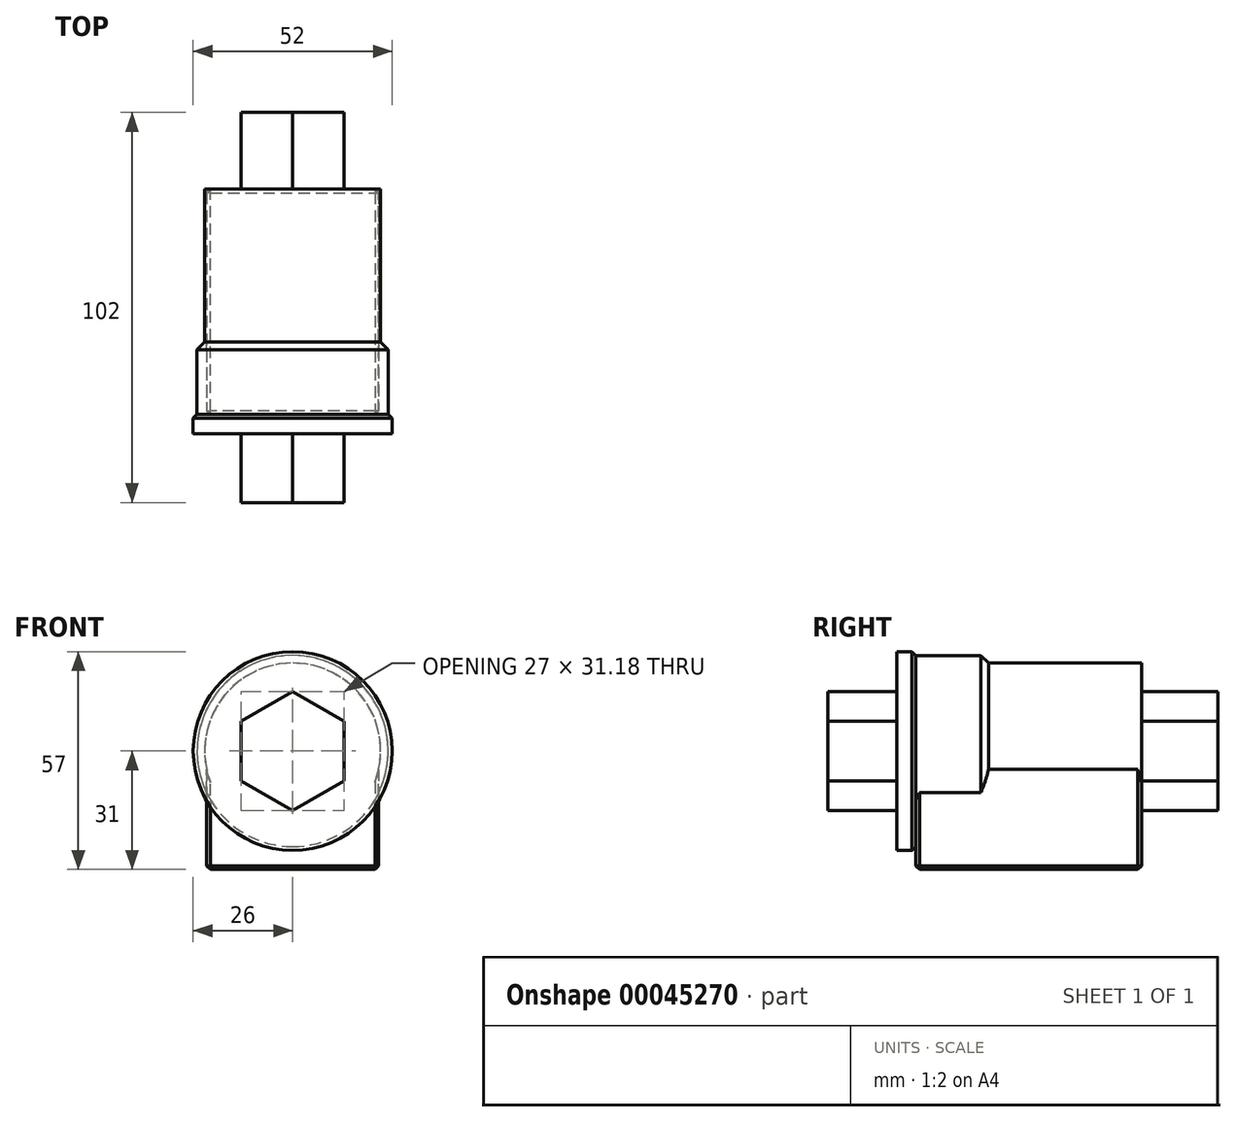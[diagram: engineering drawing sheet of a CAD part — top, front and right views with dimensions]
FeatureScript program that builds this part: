
annotation { "Feature Type Name" : "Feature", "Feature Type Description" : "" }
export const myFeature = defineFeature(function(context is Context, id is Id, definition is map)
    precondition{}
    {
        {
            var Q0;
            Q0=qCreatedBy(makeId("Front.planeOp"),FACE);
            var sketch = newSketch(context, id + "F0", { "sketchPlane" : qUnion([Q0])});
            skCircle(sketch, "E0", {"center": v(0, 0) * mm, "radius": 23 * mm});
            skCircle(sketch, "E1", {"center": v(0, 0) * mm, "radius": 26 * mm});
            skCircle(sketch, "E2", {"center": v(0, 0) * mm, "radius": 25 * mm});
            skCircle(sketch, "E3.cCircle", {"center": v(0, 0) * mm, "radius": 13.5 * mm, "construction": true});
            skLineSegment(sketch, "E3.0", {"start": v(13.5, 7.8) * mm, "end": v(13.5, -7.8) * mm});
            skLineSegment(sketch, "E3.1", {"start": v(13.5, -7.8) * mm, "end": v(0, -15.59) * mm});
            skLineSegment(sketch, "E3.2", {"start": v(0, -15.59) * mm, "end": v(-13.5, -7.8) * mm});
            skLineSegment(sketch, "E3.3", {"start": v(-13.5, -7.8) * mm, "end": v(-13.5, 7.8) * mm});
            skLineSegment(sketch, "E3.4", {"start": v(-13.5, 7.8) * mm, "end": v(0, 15.59) * mm});
            skLineSegment(sketch, "E3.5", {"start": v(0, 15.59) * mm, "end": v(13.5, 7.8) * mm});
            skPoint(sketch, "E3.0.midPoint", {"position": v(13.5, 0) * mm});
            skSolve(sketch);
        }
        {
            var Q0;
            Q0=makeQuery(id+"F0.imprint","IMPRINT",FACE,{"disambiguationData":[TD([[makeQuery(id+"F0.imprint","IMPRINT",EDGE,{"derivedFrom":sQuery(id+"F0.wireOp",EDGE,"E1")}),1.0]])]});
            var Q1;
            Q1=makeQuery(id+"F0.imprint","IMPRINT",FACE,{"disambiguationData":[TD([[makeQuery(id+"F0.imprint","IMPRINT",EDGE,{"derivedFrom":sQuery(id+"F0.wireOp",EDGE,"E0")}),-1.0]])]});
            var Q2;
            Q2=makeQuery(id+"F0.imprint","IMPRINT",FACE,{"disambiguationData":[TD([[makeQuery(id+"F0.imprint","IMPRINT",EDGE,{"derivedFrom":sQuery(id+"F0.wireOp",EDGE,"E0")}),1.0]])]});
            extrude(context, id + "F1", {"entities" : qUnion([Q0, Q1, Q2]), "depth" : 6 * mm});
        }
        {
            var Q0;
            {var subQ0=sQuery(id+"F0.wireOp",EDGE,"E3.5");var subQ1=sQuery(id+"F0.wireOp",EDGE,"E0");var subQ2=makeQuery(id+"F0.imprint","INTERSECT",VERTEX,{"disambiguationData":[OD(0.0)],"derivedFrom":[subQ1,subQ0]});Q0=makeQuery(id+"F0.imprint","IMPRINT",FACE,{"disambiguationData":[TD([[makeQuery(id+"F0.imprint","IMPRINT",EDGE,{"disambiguationData":[TD([[subQ2,-1.0]])],"derivedFrom":subQ1}),1.0]])]});}
            var Q1;
            {var subQ0=sQuery(id+"F0.wireOp",EDGE,"E3.4");var subQ1=sQuery(id+"F0.wireOp",EDGE,"E0");var subQ2=makeQuery(id+"F0.imprint","INTERSECT",VERTEX,{"disambiguationData":[OD(0.0)],"derivedFrom":[subQ1,subQ0]});Q1=makeQuery(id+"F0.imprint","IMPRINT",FACE,{"disambiguationData":[TD([[makeQuery(id+"F0.imprint","IMPRINT",EDGE,{"disambiguationData":[TD([[subQ2,-1.0]])],"derivedFrom":subQ1}),1.0]])]});}
            var Q2;
            {var subQ0=sQuery(id+"F0.wireOp",EDGE,"E3.3");var subQ1=sQuery(id+"F0.wireOp",EDGE,"E0");var subQ2=makeQuery(id+"F0.imprint","INTERSECT",VERTEX,{"disambiguationData":[OD(0.0)],"derivedFrom":[subQ1,subQ0]});Q2=makeQuery(id+"F0.imprint","IMPRINT",FACE,{"disambiguationData":[TD([[makeQuery(id+"F0.imprint","IMPRINT",EDGE,{"disambiguationData":[TD([[subQ2,-1.0]])],"derivedFrom":subQ1}),1.0]])]});}
            var Q3;
            {var subQ0=sQuery(id+"F0.wireOp",EDGE,"E3.2");var subQ1=sQuery(id+"F0.wireOp",EDGE,"E0");var subQ2=makeQuery(id+"F0.imprint","INTERSECT",VERTEX,{"disambiguationData":[OD(0.0)],"derivedFrom":[subQ1,subQ0]});Q3=makeQuery(id+"F0.imprint","IMPRINT",FACE,{"disambiguationData":[TD([[makeQuery(id+"F0.imprint","IMPRINT",EDGE,{"disambiguationData":[TD([[subQ2,-1.0]])],"derivedFrom":subQ1}),1.0]])]});}
            var Q4;
            {var subQ0=sQuery(id+"F0.wireOp",EDGE,"E3.1");var subQ1=sQuery(id+"F0.wireOp",EDGE,"E0");var subQ2=makeQuery(id+"F0.imprint","INTERSECT",VERTEX,{"disambiguationData":[OD(0.0)],"derivedFrom":[subQ1,subQ0]});Q4=makeQuery(id+"F0.imprint","IMPRINT",FACE,{"disambiguationData":[TD([[makeQuery(id+"F0.imprint","IMPRINT",EDGE,{"disambiguationData":[TD([[subQ2,-1.0]])],"derivedFrom":subQ1}),1.0]])]});}
            var Q5;
            {var subQ0=sQuery(id+"F0.wireOp",EDGE,"E3.0");var subQ1=sQuery(id+"F0.wireOp",EDGE,"E0");var subQ2=makeQuery(id+"F0.imprint","INTERSECT",VERTEX,{"disambiguationData":[OD(0.0)],"derivedFrom":[subQ1,subQ0]});Q5=makeQuery(id+"F0.imprint","IMPRINT",FACE,{"disambiguationData":[TD([[makeQuery(id+"F0.imprint","IMPRINT",EDGE,{"disambiguationData":[TD([[subQ2,1.0]])],"derivedFrom":subQ1}),1.0]])]});}
            extrude(context, id + "F2", {"entities" : qUnion([Q0, Q1, Q2, Q3, Q4, Q5]), "operationType" : NewBodyOperationType.ADD, "oppositeDirection" : true, "depth" : 58 * mm});
        }
        {
            var Q0;
            Q0=makeQuery(id+"F0.imprint","IMPRINT",FACE,{"disambiguationData":[TD([[makeQuery(id+"F0.imprint","IMPRINT",EDGE,{"derivedFrom":sQuery(id+"F0.wireOp",EDGE,"E0")}),-1.0]])]});
            extrude(context, id + "F3", {"entities" : qUnion([Q0]), "operationType" : NewBodyOperationType.ADD, "oppositeDirection" : true, "depth" : 18 * mm});
        }
        {
            var Q0;
            Q0=makeQuery(id+"F0.imprint","IMPRINT",FACE,{"disambiguationData":[TD([[makeQuery(id+"F0.imprint","IMPRINT",EDGE,{"derivedFrom":sQuery(id+"F0.wireOp",EDGE,"E3.0")}),-1.0]])]});
            extrude(context, id + "F4", {"entities" : qUnion([Q0]), "operationType" : NewBodyOperationType.ADD, "depth" : 24 * mm, "hasSecondDirection" : true, "secondDirectionOppositeDirection" : true, "secondDirectionDepth" : 78 * mm});
        }
        {
            var Q0;
            Q0=qCreatedBy(makeId("Top.planeOp"),FACE);
            var sketch = newSketch(context, id + "F5", { "sketchPlane" : qUnion([Q0])});
            skLineSegment(sketch, "E4.bottom", {"start": v(22.5, 58) * mm, "end": v(-22.5, 58) * mm});
            skLineSegment(sketch, "E4.top", {"start": v(22.5, -1) * mm, "end": v(-22.5, -1) * mm});
            skLineSegment(sketch, "E4.left", {"start": v(22.5, 58) * mm, "end": v(22.5, -1) * mm});
            skLineSegment(sketch, "E4.right", {"start": v(-22.5, 58) * mm, "end": v(-22.5, -1) * mm});
            skPoint(sketch, "E5", {"position": v(0, -1) * mm});
            skSolve(sketch);
        }
        {
            var Q0;
            Q0=makeQuery(id+"F1.opExtrude","CAP_EDGE",EDGE,{"disambiguationData":[OSD([sQuery(id+"F0.wireOp",EDGE,"E1")])],"isStart":true});
            chamfer(context, id + "F6", {"entities" : qUnion([Q0]), "width" : 2 * mm, "tangentPropagation" : true});
        }
        {
            var Q0;
            Q0=makeQuery(id+"F5.imprint","IMPRINT",FACE,{"disambiguationData":[TD([[makeQuery(id+"F5.imprint","IMPRINT",EDGE,{"derivedFrom":sQuery(id+"F5.wireOp",EDGE,"E4.bottom")}),1.0]])]});
            extrude(context, id + "F7", {"entities" : qUnion([Q0]), "operationType" : NewBodyOperationType.ADD, "oppositeDirection" : true, "depth" : 31 * mm});
        }
        {
            var Q0;
            Q0=makeQuery(id+"F3.opExtrude","CAP_EDGE",EDGE,{"disambiguationData":[OSD([sQuery(id+"F0.wireOp",EDGE,"E2")])],"isStart":false});
            chamfer(context, id + "F8", {"entities" : qUnion([Q0]), "width" : 2 * mm, "tangentPropagation" : true});
        }
        {
            var Q0;
            Q0=makeQuery(id+"F7.opExtrude","CAP_EDGE",EDGE,{"disambiguationData":[OSD([sQuery(id+"F5.wireOp",EDGE,"E4.top")])],"isStart":false});
            var Q1;
            Q1=makeQuery(id+"F7.opExtrude","CAP_EDGE",EDGE,{"disambiguationData":[OSD([sQuery(id+"F5.wireOp",EDGE,"E4.bottom")])],"isStart":false});
            var Q2;
            Q2=makeQuery(id+"F7.opExtrude","CAP_EDGE",EDGE,{"disambiguationData":[OSD([sQuery(id+"F5.wireOp",EDGE,"E4.left")])],"isStart":false});
            var Q3;
            Q3=makeQuery(id+"F7.opExtrude","CAP_EDGE",EDGE,{"disambiguationData":[OSD([sQuery(id+"F5.wireOp",EDGE,"E4.right")])],"isStart":false});
            var Q4;
            Q4=makeQuery(id+"F7.opExtrude","SWEPT_EDGE",EDGE,{"disambiguationData":[OSD([sQuery(id+"F5.wireOp",EDGE,"E4.bottom"),sQuery(id+"F5.wireOp",EDGE,"E4.right")])]});
            var Q5;
            Q5=makeQuery(id+"F7.opExtrude","SWEPT_EDGE",EDGE,{"disambiguationData":[OSD([sQuery(id+"F5.wireOp",EDGE,"E4.bottom"),sQuery(id+"F5.wireOp",EDGE,"E4.left")])]});
            var Q6;
            Q6=makeQuery(id+"F7.opExtrude","SWEPT_EDGE",EDGE,{"disambiguationData":[OSD([sQuery(id+"F5.wireOp",EDGE,"E4.top"),sQuery(id+"F5.wireOp",EDGE,"E4.right")])]});
            var Q7;
            Q7=makeQuery(id+"F7.opExtrude","SWEPT_EDGE",EDGE,{"disambiguationData":[OSD([sQuery(id+"F5.wireOp",EDGE,"E4.top"),sQuery(id+"F5.wireOp",EDGE,"E4.left")])]});
            chamfer(context, id + "F9", {"entities" : qUnion([Q0, Q1, Q2, Q3, Q4, Q5, Q6, Q7]), "chamferType" : ChamferType.TWO_OFFSETS, "width1" : 1 * mm, "oppositeDirection" : false, "width2" : 1 * mm, "tangentPropagation" : true});
        }
    });
